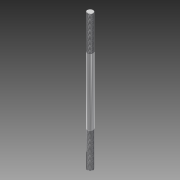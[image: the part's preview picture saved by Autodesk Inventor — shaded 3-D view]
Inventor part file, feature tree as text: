
AUTODESK INVENTOR PART (.ipt)
format: ipt  version: 2011 (Build 150229000, 229)  size: 75,776 bytes
history: native  units: mm (DEFAULTED — no unit token found)
features: thread x2, extrude x1, chamfer x1, sketch x1
ambient origin geometry x8: Origin, YZ Plane, XZ Plane, XY Plane, X Axis, Y Axis, Z Axis, Center Point
feature tree (5):
  extrude  "Extrusion1"  Depth=118.0mm TaperAngle=0.0deg
  chamfer  "Chamfer1"  Distance=0.25mm
  thread  "Thread1"  [1 undecoded]
  thread  "Thread2"  [1 undecoded]
  sketch  "Sketch1"  dims[d0=5.0mm d1=118.0mm d2=0.0mm d3=0.25mm d4=0.25mm d5=30.0mm d6=0.0mm d7=45.0deg d8=30.0mm d9=0.0mm]
note: 2 required parameter values undecoded (feature->parameter linkage not recoverable at this tier; creation-order binding heuristic only, values carry confidence <= 0.55)
